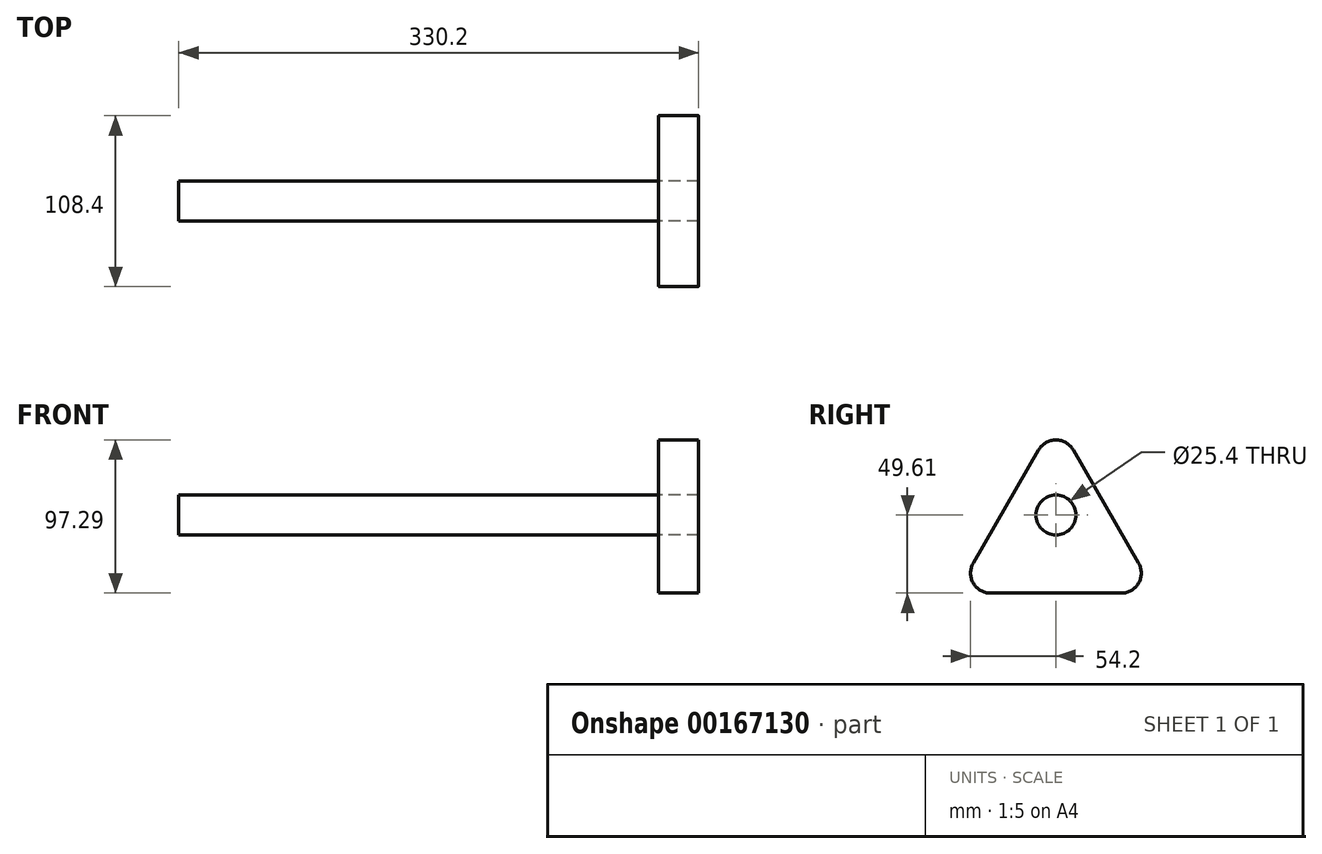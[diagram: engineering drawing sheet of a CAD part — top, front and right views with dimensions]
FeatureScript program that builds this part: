
annotation { "Feature Type Name" : "Feature", "Feature Type Description" : "" }
export const myFeature = defineFeature(function(context is Context, id is Id, definition is map)
    precondition{}
    {
        {
            var Q0;
            Q0=qCreatedBy(makeId("Right.planeOp"),FACE);
            var sketch = newSketch(context, id + "F0", { "sketchPlane" : qUnion([Q0])});
            skLineSegment(sketch, "E0", {"start": v(-63.5, -87.99) * mm, "end": v(63.5, -87.99) * mm});
            skLineSegment(sketch, "E1", {"start": v(63.5, -87.99) * mm, "end": v(0, 22) * mm});
            skLineSegment(sketch, "E2", {"start": v(-63.5, -87.99) * mm, "end": v(0, 22) * mm});
            skCircle(sketch, "E3", {"center": v(0, -38.38) * mm, "radius": 12.7 * mm});
            skPoint(sketch, "E3.centerSnap0", {"position": v(0, -87.99) * mm});
            skSolve(sketch);
        }
        {
            var Q0;
            Q0 = qSketchRegion(id + "F0", true);
            extrude(context, id + "F1", {"entities" : qUnion([Q0]), "endBound" : BoundingType.SYMMETRIC, "depth" : 25.4 * mm});
        }
        {
            var Q0;
            Q0=makeQuery(id+"F1.opExtrude","CAP_FACE",FACE,{"disambiguationData":[OSD([sQuery(id+"F0.wireOp",EDGE,"E0"),sQuery(id+"F0.wireOp",EDGE,"E1"),sQuery(id+"F0.wireOp",EDGE,"E2"),sQuery(id+"F0.wireOp",EDGE,"E3")])],"isStart":true});
            var sketch = newSketch(context, id + "F2", { "sketchPlane" : qUnion([Q0])});
            skSolve(sketch);
        }
        {
            var Q0;
            Q0=makeQuery(id+"F2.imprint","IMPRINT",FACE,{"disambiguationData":[TD([[makeQuery(id+"F2.imprint","IMPRINT",EDGE,{"derivedFrom":makeQuery(id+"F1.opExtrude","CAP_EDGE",EDGE,{"disambiguationData":[OSD([sQuery(id+"F0.wireOp",EDGE,"E3")])],"isStart":true})}),-1.0]])]});
            extrude(context, id + "F3", {"entities" : qUnion([Q0]), "depth" : 304.8 * mm});
        }
        {
            var Q0;
            Q0=makeQuery(id+"F1.opExtrude","SWEPT_EDGE",EDGE,{"disambiguationData":[OSD([sQuery(id+"F0.wireOp",EDGE,"E0"),sQuery(id+"F0.wireOp",EDGE,"E1")])]});
            var Q1;
            Q1=makeQuery(id+"F1.opExtrude","SWEPT_EDGE",EDGE,{"disambiguationData":[OSD([sQuery(id+"F0.wireOp",EDGE,"E0"),sQuery(id+"F0.wireOp",EDGE,"E2")])]});
            var Q2;
            Q2=makeQuery(id+"F1.opExtrude","SWEPT_EDGE",EDGE,{"disambiguationData":[OSD([sQuery(id+"F0.wireOp",EDGE,"E1"),sQuery(id+"F0.wireOp",EDGE,"E2")])]});
            fillet(context, id + "F4", {"entities" : qUnion([Q0, Q1, Q2]), "radius" : 12.7 * mm, "tangentPropagation" : true, "allowEdgeOverflow" : false});
        }
    });
